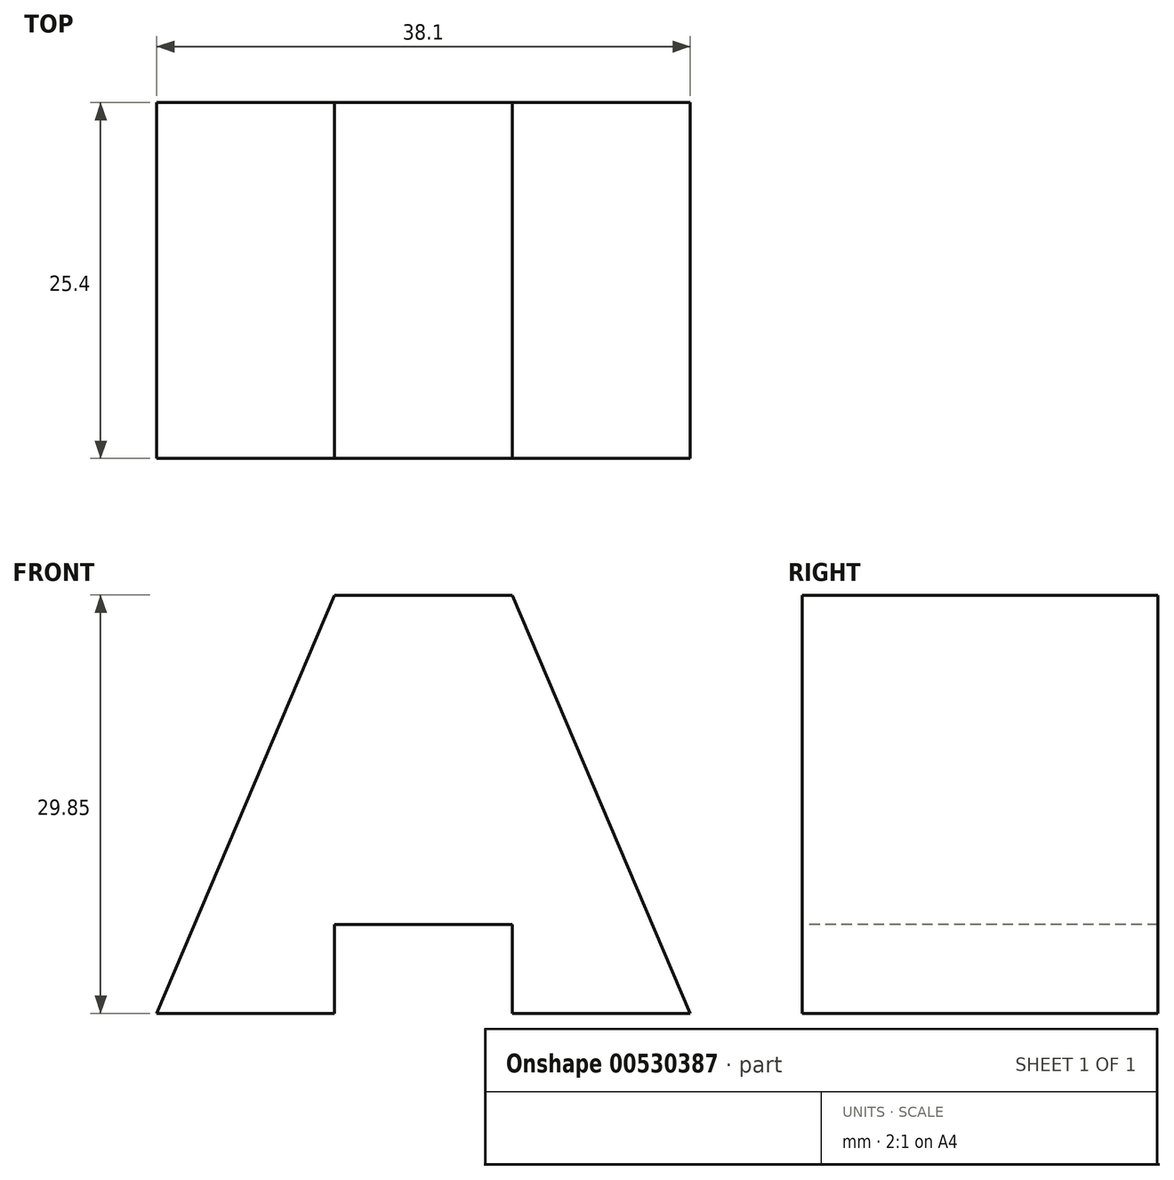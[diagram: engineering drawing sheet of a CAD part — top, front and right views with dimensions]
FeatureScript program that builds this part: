
annotation { "Feature Type Name" : "Feature", "Feature Type Description" : "" }
export const myFeature = defineFeature(function(context is Context, id is Id, definition is map)
    precondition{}
    {
        {
            var Q0;
            Q0=qCreatedBy(makeId("Front.planeOp"),FACE);
            var sketch = newSketch(context, id + "F0", { "sketchPlane" : qUnion([Q0])});
            skLineSegment(sketch, "E0", {"start": v(-29.37, 0) * mm, "end": v(-16.67, 29.85) * mm});
            skLineSegment(sketch, "E1", {"start": v(-16.67, 29.85) * mm, "end": v(-3.97, 29.85) * mm});
            skLineSegment(sketch, "E2", {"start": v(-3.97, 29.85) * mm, "end": v(8.73, 0) * mm});
            skLineSegment(sketch, "E3", {"start": v(8.73, 0) * mm, "end": v(-29.37, 0) * mm});
            skSolve(sketch);
        }
        {
            var Q0;
            Q0=makeQuery(id+"F0.imprint","IMPRINT",FACE,{"disambiguationData":[TD([[makeQuery(id+"F0.imprint","IMPRINT",EDGE,{"derivedFrom":sQuery(id+"F0.wireOp",EDGE,"E0")}),-1.0]])]});
            extrude(context, id + "F1", {"entities" : qUnion([Q0]), "depth" : 25.4 * mm, "offsetDistance" : 25.4 * mm});
        }
        {
            var Q0;
            Q0=makeQuery(id+"F1.opExtrude","CAP_FACE",FACE,{"disambiguationData":[OSD([sQuery(id+"F0.wireOp",EDGE,"E0"),sQuery(id+"F0.wireOp",EDGE,"E1"),sQuery(id+"F0.wireOp",EDGE,"E2"),sQuery(id+"F0.wireOp",EDGE,"E3")])],"isStart":false});
            var sketch = newSketch(context, id + "F2", { "sketchPlane" : qUnion([Q0])});
            skLineSegment(sketch, "E4", {"start": v(-29.37, 0) * mm, "end": v(-16.67, 0) * mm});
            skLineSegment(sketch, "E5", {"start": v(-16.67, 0) * mm, "end": v(-16.67, 6.35) * mm});
            skLineSegment(sketch, "E6", {"start": v(-16.67, 6.35) * mm, "end": v(-3.97, 6.35) * mm});
            skLineSegment(sketch, "E7", {"start": v(-3.97, 6.35) * mm, "end": v(-3.97, 0) * mm});
            skLineSegment(sketch, "E8", {"start": v(-3.97, 0) * mm, "end": v(8.73, 0) * mm});
            skLineSegment(sketch, "E9", {"start": v(-3.97, 0) * mm, "end": v(-16.67, 0) * mm});
            skSolve(sketch);
        }
        {
            var Q0;
            Q0=makeQuery(id+"F2.imprint","IMPRINT",FACE,{"disambiguationData":[TD([[makeQuery(id+"F2.imprint","IMPRINT",EDGE,{"derivedFrom":sQuery(id+"F2.wireOp",EDGE,"E5")}),-1.0]])]});
            extrude(context, id + "F3", {"entities" : qUnion([Q0]), "operationType" : NewBodyOperationType.REMOVE, "endBound" : BoundingType.THROUGH_ALL, "oppositeDirection" : true, "depth" : 25.4 * mm, "offsetDistance" : 25.4 * mm});
        }
    });
